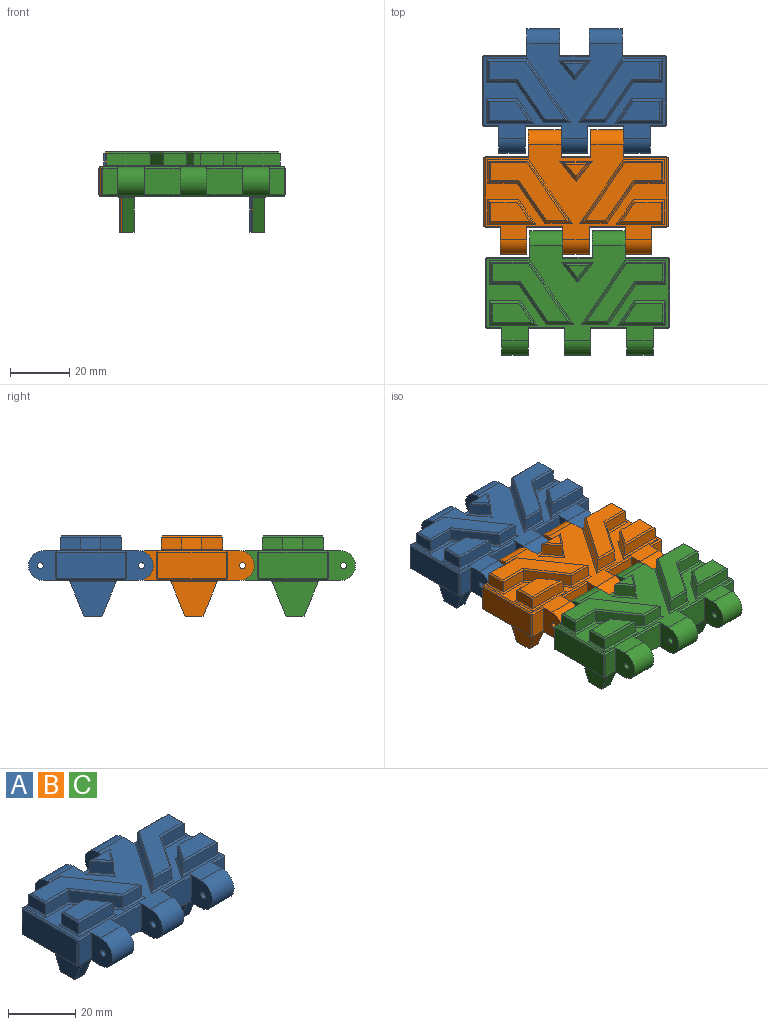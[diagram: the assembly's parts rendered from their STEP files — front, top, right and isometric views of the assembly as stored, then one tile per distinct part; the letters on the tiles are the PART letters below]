
ASSEMBLY  parts=3 mates=2
PART A: 145 faces, bbox 62x42x27 mm
  f0: plane 61x32mm, normal (0,0,1), area 857.2mm2, adj f3,f4,f6,f7,f11,f12,f14,f15
  f1: plane 23x9mm, normal (1,0,0), area 207mm2, adj f86,f87,f88,f89
  f2: plane 14.5x9mm, normal (0,1,0), area 130.5mm2, adj f3,f87,f106,f111
  f3: plane 10x9.5mm, normal (1,0,0), area 76.4mm2, adj f0,f2,f20,f76,f81,f106,f111
  f4: plane 10x9.5mm, normal (-1,0,0), area 76.4mm2, adj f0,f5,f20,f76,f81,f105,f112
  f5: plane 10x9mm, normal (0,1,0), area 90mm2, adj f4,f6,f105,f112
  f6: plane 10x9.5mm, normal (1,0,0), area 76.4mm2, adj f0,f5,f20,f75,f80,f105,f112
  f7: plane 10x9.5mm, normal (-1,0,0), area 76.4mm2, adj f0,f8,f20,f75,f80,f104,f113
  f8: plane 14.5x9mm, normal (0,1,0), area 130.5mm2, adj f7,f84,f104,f113
  f9: plane 23x9mm, normal (-1,0,0), area 207mm2, adj f82,f83,f84,f85
  f10: plane 9x5mm, normal (0,-1,0), area 45mm2, adj f11,f83,f100,f110
  f11: plane 10x9.5mm, normal (-1,0,0), area 76.4mm2, adj f0,f10,f20,f74,f79,f100,f110
  f12: plane 10x9.5mm, normal (1,0,0), area 76.4mm2, adj f0,f13,f20,f74,f79,f101,f109
  f13: plane 12x9mm, normal (0,-1,0), area 108mm2, adj f12,f14,f101,f109
  f14: plane 10x9.5mm, normal (-1,0,0), area 76.4mm2, adj f0,f13,f20,f73,f78,f101,f109
  f15: plane 10x9.5mm, normal (1,0,0), area 76.4mm2, adj f0,f16,f20,f73,f78,f102,f108
  f16: plane 12x9mm, normal (0,-1,0), area 108mm2, adj f15,f17,f102,f108
  f17: plane 10x9.5mm, normal (-1,0,0), area 76.4mm2, adj f0,f16,f20,f72,f77,f102,f108
  f18: plane 10x9.5mm, normal (1,0,0), area 76.4mm2, adj f0,f19,f20,f72,f77,f103,f107
  f19: plane 9x5mm, normal (0,-1,0), area 45mm2, adj f18,f88,f103,f107
  f20: plane 61x32mm, normal (0,0,-1), area 1456.8mm2, adj f3,f4,f6,f7,f11,f12,f14,f15
  f21: plane 8.76x4mm, normal (0,1,0), area 35mm2, adj f22,f23,f59,f132
  f22: plane 5.59x4.38mm, normal (-0.79,-0.62,0), area 28.4mm2, adj f21,f23,f60,f133
  f23: plane 5.59x4.38mm, normal (0.79,-0.62,0), area 28.4mm2, adj f21,f22,f61,f134
  f24: plane 6.7x4.28mm, normal (0,0,1), area 14.3mm2, adj f59,f60,f61
  f25: plane 9.7x4mm, normal (0,1,0), area 38.8mm2, adj f26,f28,f71,f123
  f26: plane 7.32x4mm, normal (-1,0,0), area 29.3mm2, adj f25,f27,f70,f125
  f27: plane 14.72x4mm, normal (0,-1,0), area 58.9mm2, adj f26,f28,f68,f124
  f28: plane 7.32x5.02mm, normal (0.82,0.57,0), area 35.5mm2, adj f25,f27,f69,f122
  f29: plane 13.27x6.32mm, normal (0,0,1), area 70.2mm2, adj f68,f69,f70,f71
  f30: plane 12.98x4mm, normal (0,1,0), area 51.9mm2, adj f31,f35,f67,f128
  f31: plane 6.85x4mm, normal (-1,0,0), area 27.4mm2, adj f30,f32,f66,f126
  f32: plane 9.7x4mm, normal (0,-1,0), area 38.8mm2, adj f31,f33,f64,f127
  f33: plane 13.59x9.32mm, normal (-0.82,-0.57,0), area 65.9mm2, adj f32,f34,f62,f129
  f34: plane 7.97x4mm, normal (0,-1,0), area 31.9mm2, adj f33,f35,f63,f131
  f35: plane 20.44x14.01mm, normal (0.82,0.57,0), area 99.1mm2, adj f30,f34,f65,f130
  f36: plane 25.54x19.44mm, normal (0,0,1), area 175mm2, adj f62,f63,f64,f65,f66,f67
  f37: plane 20.44x14.01mm, normal (-0.82,0.57,0), area 99.1mm2, adj f38,f42,f57,f140
  f38: plane 7.97x4mm, normal (0,-1,0), area 31.9mm2, adj f37,f39,f58,f138
  f39: plane 13.59x9.32mm, normal (0.82,-0.57,0), area 65.9mm2, adj f38,f40,f56,f136
  f40: plane 9.7x4mm, normal (0,-1,0), area 38.8mm2, adj f39,f41,f54,f135
  f41: plane 6.85x4mm, normal (1,0,0), area 27.4mm2, adj f40,f42,f53,f137
  f42: plane 12.98x4mm, normal (0,1,0), area 51.9mm2, adj f37,f41,f55,f139
  f43: plane 25.54x19.44mm, normal (0,0,1), area 175mm2, adj f53,f54,f55,f56,f57,f58
  f44: plane 14.72x4mm, normal (0,-1,0), area 58.9mm2, adj f45,f47,f51,f142
  f45: plane 7.32x4mm, normal (1,0,0), area 29.3mm2, adj f44,f46,f52,f141
  f46: plane 9.7x4mm, normal (0,1,0), area 38.8mm2, adj f45,f47,f50,f143
  f47: plane 7.32x5.02mm, normal (-0.82,0.57,0), area 35.5mm2, adj f44,f46,f49,f144
  f48: plane 13.27x6.32mm, normal (0,0,1), area 70.2mm2, adj f49,f50,f51,f52
  f49: plane 7.32x5.28mm, normal (-0.58,0.4,0.71), area 5.8mm2, adj f47,f48,f50,f51
  f50: plane 9.7x0.5mm, normal (0,0.71,0.71), area 6.6mm2, adj f46,f48,f49,f52
  f51: plane 14.72x0.5mm, normal (0,-0.71,0.71), area 9.9mm2, adj f44,f48,f49,f52
  f52: plane 7.32x0.5mm, normal (0.71,0,0.71), area 4.8mm2, adj f45,f48,f50,f51
  f53: plane 6.85x0.5mm, normal (0.71,0,0.71), area 4.5mm2, adj f41,f43,f54,f55
  f54: plane 9.97x0.5mm, normal (0,-0.71,0.71), area 6.8mm2, adj f40,f43,f53,f56
  f55: plane 12.98x0.5mm, normal (0,0.71,0.71), area 8.9mm2, adj f42,f43,f53,f57
  f56: plane 14.09x9.58mm, normal (0.58,-0.4,0.71), area 11.7mm2, adj f39,f43,f54,f58
  f57: plane 20.44x14.27mm, normal (-0.58,0.4,0.71), area 17.1mm2, adj f37,f43,f55,f58
  f58: plane 7.97x0.5mm, normal (0,-0.71,0.71), area 5.2mm2, adj f38,f43,f56,f57
  f59: plane 8.76x0.5mm, normal (0,0.71,0.71), area 5.5mm2, adj f21,f24,f60,f61
  f60: plane 5.59x4.38mm, normal (-0.56,-0.44,0.71), area 4.4mm2, adj f22,f24,f59,f61
  f61: plane 5.59x4.38mm, normal (0.56,-0.44,0.71), area 4.4mm2, adj f23,f24,f59,f60
  f62: plane 14.09x9.58mm, normal (-0.58,-0.4,0.71), area 11.7mm2, adj f33,f36,f63,f64
  f63: plane 7.97x0.5mm, normal (0,-0.71,0.71), area 5.2mm2, adj f34,f36,f62,f65
  f64: plane 9.97x0.5mm, normal (0,-0.71,0.71), area 6.8mm2, adj f32,f36,f62,f66
  f65: plane 20.44x14.27mm, normal (0.58,0.4,0.71), area 17.1mm2, adj f35,f36,f63,f67
  f66: plane 6.85x0.5mm, normal (-0.71,0,0.71), area 4.5mm2, adj f31,f36,f64,f67
  f67: plane 12.98x0.5mm, normal (0,0.71,0.71), area 8.9mm2, adj f30,f36,f65,f66
  f68: plane 14.72x0.5mm, normal (0,-0.71,0.71), area 9.9mm2, adj f27,f29,f69,f70
  f69: plane 7.32x5.28mm, normal (0.58,0.4,0.71), area 5.8mm2, adj f28,f29,f68,f71
  f70: plane 7.32x0.5mm, normal (-0.71,0,0.71), area 4.8mm2, adj f26,f29,f68,f71
  f71: plane 9.7x0.5mm, normal (0,0.71,0.71), area 6.6mm2, adj f25,f29,f69,f70
  f72: cylinder r=5mm len=10mm, axis (-1,0,0), area 141.4mm2, adj f0,f17,f18,f20
  f73: cylinder r=5mm len=10mm, axis (-1,0,0), area 141.4mm2, adj f0,f14,f15,f20
  f74: cylinder r=5mm len=10mm, axis (-1,0,0), area 141.4mm2, adj f0,f11,f12,f20
  f75: cylinder r=5mm len=11mm, axis (1,0,0), area 172.8mm2, adj f0,f6,f7,f20
  f76: cylinder r=5mm len=11mm, axis (1,0,0), area 172.8mm2, adj f0,f3,f4,f20
  f77: cylinder r=1mm len=9mm, axis (1,0,0), area 56.5mm2, adj f17,f18
  f78: cylinder r=1mm len=9mm, axis (1,0,0), area 56.5mm2, adj f14,f15
  f79: cylinder r=1mm len=9mm, axis (1,0,0), area 56.5mm2, adj f11,f12
  f80: cylinder r=1mm len=11mm, axis (1,0,0), area 69.1mm2, adj f6,f7
  f81: cylinder r=1mm len=11mm, axis (1,0,0), area 69.1mm2, adj f3,f4
  f82: plane 23.5x0.5mm, normal (-0.71,0,-0.71), area 16.4mm2, adj f9,f20,f83,f84,f110,f113
  f83: plane 9.5x0.5mm, normal (-0.71,-0.71,0), area 6.5mm2, adj f9,f10,f82,f85,f100,f110
  f84: plane 9.5x0.5mm, normal (-0.71,0.71,0), area 6.5mm2, adj f8,f9,f82,f85,f104,f113
  f85: plane 23.5x0.5mm, normal (-0.71,0,0.71), area 16.4mm2, adj f0,f9,f83,f84,f100,f104
  f86: plane 23.5x0.5mm, normal (0.71,0,0.71), area 16.4mm2, adj f0,f1,f87,f88,f103,f106
  f87: plane 9.5x0.5mm, normal (0.71,0.71,0), area 6.5mm2, adj f1,f2,f86,f89,f106,f111
  f88: plane 9.5x0.5mm, normal (0.71,-0.71,0), area 6.5mm2, adj f1,f19,f86,f89,f103,f107
  f89: plane 23.5x0.5mm, normal (0.71,0,-0.71), area 16.4mm2, adj f1,f20,f87,f88,f107,f111
  f90: plane 15.58x11.5mm, normal (-1,0,0), area 124.1mm2, adj f92,f96,f97,f115
  f91: plane 15.58x11.5mm, normal (1,0,0), area 124.1mm2, adj f92,f96,f97,f116
  f92: plane 6x4mm, normal (0,0,-1), area 24mm2, adj f90,f91,f96,f97
  f93: plane 15.58x11.5mm, normal (1,0,0), area 124.1mm2, adj f95,f98,f99,f119
  f94: plane 15.58x11.5mm, normal (-1,0,0), area 124.1mm2, adj f95,f98,f99,f120
  f95: plane 6x4mm, normal (0,0,-1), area 24mm2, adj f93,f94,f98,f99
  f96: plane 11.69x4.87mm, normal (0,0.92,-0.38), area 50.7mm2, adj f90,f91,f92,f115,f116,f117
  f97: plane 11.69x4.87mm, normal (0,-0.92,-0.38), area 50.7mm2, adj f90,f91,f92,f114,f115,f116
  f98: plane 11.69x4.87mm, normal (0,-0.92,-0.38), area 50.7mm2, adj f93,f94,f95,f119,f120,f121
  f99: plane 11.69x4.87mm, normal (0,0.92,-0.38), area 50.7mm2, adj f93,f94,f95,f118,f119,f120
  f100: plane 5.25x0.5mm, normal (0,-0.71,0.71), area 3.6mm2, adj f0,f10,f11,f83,f85
  f101: plane 12x0.5mm, normal (0,-0.71,0.71), area 8.5mm2, adj f0,f12,f13,f14
  f102: plane 12x0.5mm, normal (0,-0.71,0.71), area 8.5mm2, adj f0,f15,f16,f17
  f103: plane 5.25x0.5mm, normal (0,-0.71,0.71), area 3.6mm2, adj f0,f18,f19,f86,f88
  f104: plane 14.75x0.5mm, normal (0,0.71,0.71), area 10.3mm2, adj f0,f7,f8,f84,f85
  f105: plane 10x0.5mm, normal (0,0.71,0.71), area 7.1mm2, adj f0,f4,f5,f6
  f106: plane 14.75x0.5mm, normal (0,0.71,0.71), area 10.3mm2, adj f0,f2,f3,f86,f87
  f107: plane 5.25x0.5mm, normal (0,-0.71,-0.71), area 3.6mm2, adj f18,f19,f20,f88,f89
  f108: plane 12x0.5mm, normal (0,-0.71,-0.71), area 8.5mm2, adj f15,f16,f17,f20
  f109: plane 12x0.5mm, normal (0,-0.71,-0.71), area 8.5mm2, adj f12,f13,f14,f20
  f110: plane 5.25x0.5mm, normal (0,-0.71,-0.71), area 3.6mm2, adj f10,f11,f20,f82,f83
  f111: plane 14.75x0.5mm, normal (0,0.71,-0.71), area 10.3mm2, adj f2,f3,f20,f87,f89
  f112: plane 10x0.5mm, normal (0,0.71,-0.71), area 7.1mm2, adj f4,f5,f6,f20
  f113: plane 14.75x0.5mm, normal (0,0.71,-0.71), area 10.3mm2, adj f7,f8,f20,f82,f84
  f114: plane 5x0.46mm, normal (0,-0.55,-0.83), area 2.6mm2, adj f20,f97,f115,f116
  f115: plane 16.67x0.5mm, normal (-0.71,0,-0.71), area 11.3mm2, adj f20,f90,f96,f97,f114,f117
  f116: plane 16.67x0.5mm, normal (0.71,0,-0.71), area 11.3mm2, adj f20,f91,f96,f97,f114,f117
  f117: plane 5x0.46mm, normal (0,0.55,-0.83), area 2.6mm2, adj f20,f96,f115,f116
  f118: plane 5x0.46mm, normal (0,0.55,-0.83), area 2.6mm2, adj f20,f99,f119,f120
  f119: plane 16.67x0.5mm, normal (0.71,0,-0.71), area 11.3mm2, adj f20,f93,f98,f99,f118,f121
  f120: plane 16.67x0.5mm, normal (-0.71,0,-0.71), area 11.3mm2, adj f20,f94,f98,f99,f118,f121
  f121: plane 5x0.46mm, normal (0,-0.55,-0.83), area 2.6mm2, adj f20,f98,f119,f120
  f122: plane 8.32x5.97mm, normal (0.58,0.4,0.71), area 6.7mm2, adj f0,f28,f123,f124
  f123: plane 10.47x0.5mm, normal (0,0.71,0.71), area 7.1mm2, adj f0,f25,f122,f125
  f124: plane 16.17x0.5mm, normal (0,-0.71,0.71), area 10.9mm2, adj f0,f27,f122,f125
  f125: plane 8.32x0.5mm, normal (-0.71,0,0.71), area 5.5mm2, adj f0,f26,f123,f124
  f126: plane 7.85x0.5mm, normal (-0.71,0,0.71), area 5.2mm2, adj f0,f31,f127,f128
  f127: plane 10.2x0.5mm, normal (0,-0.71,0.71), area 6.9mm2, adj f0,f32,f126,f129
  f128: plane 13.74x0.5mm, normal (0,0.71,0.71), area 9.4mm2, adj f0,f30,f126,f130
  f129: plane 14.09x9.58mm, normal (-0.58,-0.4,0.71), area 11.7mm2, adj f0,f33,f127,f131
  f130: plane 21.44x14.96mm, normal (0.58,0.4,0.71), area 18mm2, adj f0,f35,f128,f131
  f131: plane 9.18x0.5mm, normal (0,-0.71,0.71), area 6.1mm2, adj f0,f34,f129,f130
  f132: plane 10.81x0.5mm, normal (0,0.71,0.71), area 6.9mm2, adj f0,f21,f133,f134
  f133: plane 6.9x5.4mm, normal (-0.56,-0.44,0.71), area 5.6mm2, adj f0,f22,f132,f134
  f134: plane 6.9x5.4mm, normal (0.56,-0.44,0.71), area 5.6mm2, adj f0,f23,f132,f133
  f135: plane 10.2x0.5mm, normal (0,-0.71,0.71), area 6.9mm2, adj f0,f40,f136,f137
  f136: plane 14.09x9.58mm, normal (0.58,-0.4,0.71), area 11.7mm2, adj f0,f39,f135,f138
  f137: plane 7.85x0.5mm, normal (0.71,0,0.71), area 5.2mm2, adj f0,f41,f135,f139
  f138: plane 9.18x0.5mm, normal (0,-0.71,0.71), area 6.1mm2, adj f0,f38,f136,f140
  f139: plane 13.74x0.5mm, normal (0,0.71,0.71), area 9.4mm2, adj f0,f42,f137,f140
  f140: plane 21.44x14.96mm, normal (-0.58,0.4,0.71), area 18mm2, adj f0,f37,f138,f139
  f141: plane 8.32x0.5mm, normal (0.71,0,0.71), area 5.5mm2, adj f0,f45,f142,f143
  f142: plane 16.17x0.5mm, normal (0,-0.71,0.71), area 10.9mm2, adj f0,f44,f141,f144
  f143: plane 10.47x0.5mm, normal (0,0.71,0.71), area 7.1mm2, adj f0,f46,f141,f144
  f144: plane 8.32x5.97mm, normal (-0.58,0.4,0.71), area 6.7mm2, adj f0,f47,f142,f143
PART B: same geometry as A
PART C: same geometry as A
PLACE A t=(8.82,8.42,8.49)mm
PLACE B t=(9.32,-25.58,8.49)mm
PLACE C t=(9.82,-59.58,8.49)mm
MATE fastened C.f80 <-> B.f77  axis (1,0,0) through (25.82,-42.58,8.49)mm
MATE fastened B.f80 <-> A.f77  axis (1,0,0) through (25.32,-8.58,8.49)mm
